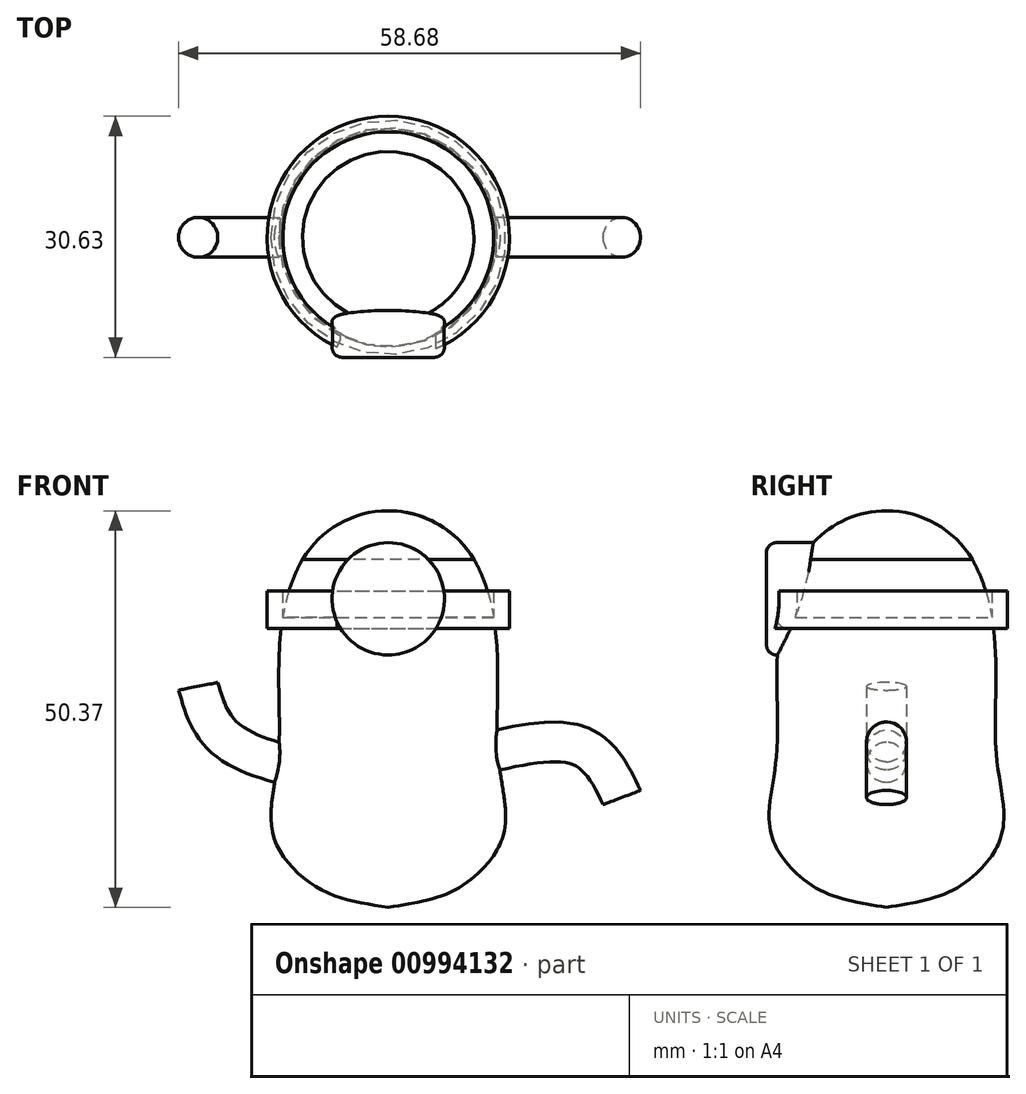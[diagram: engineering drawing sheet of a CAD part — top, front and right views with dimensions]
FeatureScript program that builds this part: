
annotation { "Feature Type Name" : "Feature", "Feature Type Description" : "" }
export const myFeature = defineFeature(function(context is Context, id is Id, definition is map)
    precondition{}
    {
        {
            var Q0;
            Q0=qCreatedBy(makeId("Front.planeOp"),FACE);
            var sketch = newSketch(context, id + "F0", { "sketchPlane" : qUnion([Q0])});
            skCircle(sketch, "E0", {"center": v(0, 37.67) * mm, "radius": 12.7 * mm});
            skFitSpline(sketch, "E1", {"points": [v(-10.9, 44.18) * mm, v(-13.9, 20.25) * mm, v(-14.64, 9.28) * mm, v(-8.66, 2.3) * mm, v(0, 0) * mm], "startDerivative": vector(-37.7, -66.61) * mm, "endDerivative": vector(42.28, -6.47) * mm});
            skLineSegment(sketch, "E2", {"start": v(0, 0) * mm, "end": v(0, 72.84) * mm});
            skFitSpline(sketch, "E3.0", {"points": [v(-12.23, 44.93) * mm, v(-13.08, 43.43) * mm, v(-14.34, 40.3) * mm, v(-15.23, 35.5) * mm, v(-15.47, 30.77) * mm, v(-15.41, 27) * mm, v(-15.35, 24.19) * mm, v(-15.34, 22.53) * mm, v(-15.37, 21.28) * mm, v(-15.4, 20.39) * mm, v(-15.48, 19.53) * mm, v(-15.6, 18.41) * mm, v(-15.78, 17.08) * mm, v(-16.02, 15.54) * mm, v(-16.25, 14.05) * mm, v(-16.41, 12.58) * mm, v(-16.46, 11.1) * mm, v(-16.34, 9.86) * mm, v(-16.12, 8.85) * mm, v(-15.8, 7.86) * mm, v(-15.27, 6.68) * mm, v(-14.44, 5.35) * mm, v(-13.1, 3.72) * mm, v(-11.52, 2.3) * mm, v(-9.78, 1.15) * mm, v(-8.4, 0.45) * mm, v(-7.03, -0.1) * mm, v(-5.18, -0.66) * mm, v(-2.89, -1.12) * mm, v(-1.1, -1.37) * mm, v(-0.23, -1.5) * mm]});
            skLineSegment(sketch, "E4", {"start": v(-0.23, -1.5) * mm, "end": v(0, 0) * mm});
            skLineSegment(sketch, "E5", {"start": v(-14.9, 11.23) * mm, "end": v(-16.2, 9.28) * mm});
            skSolve(sketch);
        }
        {
            var Q0;
            {var subQ0=sQuery(id+"F0.wireOp",EDGE,"E1");var subQ1=sQuery(id+"F0.wireOp",EDGE,"E0");var subQ2=makeQuery(id+"F0.imprint","INTERSECT",VERTEX,{"disambiguationData":[OD(0.0)],"derivedFrom":[subQ1,subQ0]});Q0=makeQuery(id+"F0.imprint","IMPRINT",FACE,{"disambiguationData":[TD([[makeQuery(id+"F0.imprint","IMPRINT",EDGE,{"disambiguationData":[TD([[subQ2,1.0]])],"derivedFrom":subQ1}),1.0]])]});}
            var Q1;
            {var subQ0=sQuery(id+"F0.wireOp",EDGE,"E1");var subQ1=sQuery(id+"F0.wireOp",EDGE,"E0");var subQ2=makeQuery(id+"F0.imprint","INTERSECT",VERTEX,{"disambiguationData":[OD(1.0)],"derivedFrom":[subQ1,subQ0]});Q1=makeQuery(id+"F0.imprint","IMPRINT",FACE,{"disambiguationData":[TD([[makeQuery(id+"F0.imprint","IMPRINT",EDGE,{"disambiguationData":[TD([[subQ2,-1.0]])],"derivedFrom":subQ1}),-1.0]])]});}
            var Q2;
            {var subQ0=sQuery(id+"F0.wireOp",EDGE,"E4");Q2=makeQuery(id+"F0.imprint","IMPRINT",FACE,{"disambiguationData":[TD([[makeQuery(id+"F0.imprint","IMPRINT",EDGE,{"derivedFrom":subQ0}),1.0]])]});}
            var Q3;
            Q3=sQuery(id+"F0.wireOp",EDGE,"E2");
            revolve(context, id + "F1", {"surfaceOperationType" : NewSurfaceOperationType.NEW, "entities" : qUnion([Q0, Q1, Q2]), "axis" : qUnion([Q3]), "revolveType" : RevolveType.FULL});
        }
        {
            var Q0;
            Q0=qCreatedBy(makeId("Front.planeOp"),FACE);
            var sketch = newSketch(context, id + "F2", { "sketchPlane" : qUnion([Q0])});
            skCircle(sketch, "E6", {"center": v(0, 39.2) * mm, "radius": 7.13 * mm});
            skSolve(sketch);
        }
        {
            var Q0;
            Q0=makeQuery(id+"F2.imprint","IMPRINT",FACE,{"disambiguationData":[TD([[makeQuery(id+"F2.imprint","IMPRINT",EDGE,{"derivedFrom":sQuery(id+"F2.wireOp",EDGE,"E6")}),1.0]])]});
            extrude(context, id + "F3", {"entities" : qUnion([Q0]), "operationType" : NewBodyOperationType.ADD, "depth" : 15.24 * mm, "offsetDistance" : 25.4 * mm});
        }
        {
            var Q0;
            Q0=qCreatedBy(makeId("Front.planeOp"),FACE);
            var sketch = newSketch(context, id + "F4", { "sketchPlane" : qUnion([Q0])});
            skLineSegment(sketch, "E7.bottom", {"start": v(-15.4, 40.2) * mm, "end": v(-13.4, 40.2) * mm});
            skLineSegment(sketch, "E7.top", {"start": v(-15.4, 35.46) * mm, "end": v(-13.4, 35.46) * mm});
            skLineSegment(sketch, "E7.left", {"start": v(-15.4, 40.2) * mm, "end": v(-15.4, 35.46) * mm});
            skLineSegment(sketch, "E7.right", {"start": v(-13.4, 40.2) * mm, "end": v(-13.4, 35.46) * mm});
            skLineSegment(sketch, "E8", {"start": v(0, 35.7) * mm, "end": v(0, 44.19) * mm});
            skSolve(sketch);
        }
        {
            var Q0;
            Q0=makeQuery(id+"F4.imprint","IMPRINT",FACE,{"disambiguationData":[TD([[makeQuery(id+"F4.imprint","IMPRINT",EDGE,{"derivedFrom":sQuery(id+"F4.wireOp",EDGE,"E7.bottom")}),-1.0]])]});
            var Q1;
            Q1=sQuery(id+"F4.wireOp",EDGE,"E8");
            revolve(context, id + "F5", {"operationType" : NewBodyOperationType.ADD, "surfaceOperationType" : NewSurfaceOperationType.NEW, "entities" : qUnion([Q0]), "axis" : qUnion([Q1]), "revolveType" : RevolveType.TWO_DIRECTIONS, "angle" : 65 * degree, "angleBack" : 100 * degree});
        }
        {
            var Q0;
            Q0=qCreatedBy(makeId("Front.planeOp"),FACE);
            var sketch = newSketch(context, id + "F6", { "sketchPlane" : qUnion([Q0])});
            skFitSpline(sketch, "E9", {"points": [v(-24.61, 27.98) * mm, v(-20.87, 21) * mm, v(-5.92, 16.76) * mm, v(10.78, 18.76) * mm, v(24.24, 20) * mm, v(29.22, 13.77) * mm], "startDerivative": vector(13.67, -47.11) * mm, "endDerivative": vector(23.23, -48.15) * mm});
            skSolve(sketch);
        }
        {
            var Q0;
            Q0=makeQuery(id+"F3.opExtrude","CAP_EDGE",EDGE,{"disambiguationData":[OSD([sQuery(id+"F2.wireOp",EDGE,"E6")])],"isStart":false});
            fillet(context, id + "F7", {"entities" : qUnion([Q0]), "radius" : 1.27 * mm, "tangentPropagation" : true, "allowEdgeOverflow" : false});
        }
        {
            var Q0;
            Q0=qCreatedBy(makeId("Right.planeOp"),FACE);
            var sketch = newSketch(context, id + "F8", { "sketchPlane" : qUnion([Q0])});
            skCircle(sketch, "E10", {"center": v(0, 17.39) * mm, "radius": 2.54 * mm});
            skSolve(sketch);
        }
        {
            var Q0;
            Q0=makeQuery(id+"F8.imprint","IMPRINT",FACE,{"disambiguationData":[TD([[makeQuery(id+"F8.imprint","IMPRINT",EDGE,{"derivedFrom":sQuery(id+"F8.wireOp",EDGE,"E10")}),1.0]])]});
            var Q1;
            Q1=sQuery(id+"F6.wireOp",EDGE,"E9");
            sweep(context, id + "F9", {"operationType" : NewBodyOperationType.ADD, "profiles" : qUnion([Q0]), "path" : qUnion([Q1])});
        }
    });
